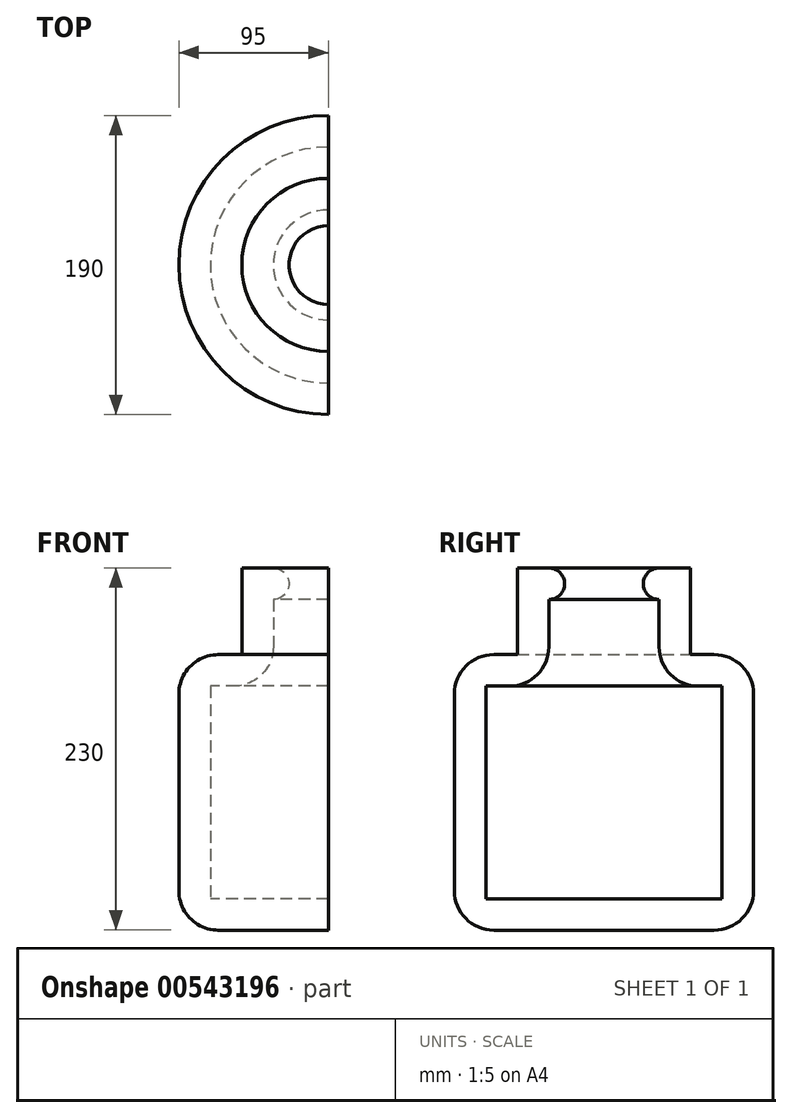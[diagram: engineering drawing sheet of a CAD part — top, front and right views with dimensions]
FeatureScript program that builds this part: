
annotation { "Feature Type Name" : "Feature", "Feature Type Description" : "" }
export const myFeature = defineFeature(function(context is Context, id is Id, definition is map)
    precondition{}
    {
        {
            var Q0;
            Q0=qCreatedBy(makeId("Front.planeOp"),FACE);
            var sketch = newSketch(context, id + "F0", { "sketchPlane" : qUnion([Q0])});
            skLineSegment(sketch, "E0", {"start": v(-40, 68.66) * mm, "end": v(-40, -56.34) * mm});
            skLineSegment(sketch, "E1", {"start": v(-15, -81.34) * mm, "end": v(55, -81.34) * mm});
            skLineSegment(sketch, "E2", {"start": v(55, -81.34) * mm, "end": v(55, -61.34) * mm});
            skLineSegment(sketch, "E3", {"start": v(55, -61.34) * mm, "end": v(-20, -61.34) * mm});
            skLineSegment(sketch, "E4", {"start": v(-20, -61.34) * mm, "end": v(-20, 73.66) * mm});
            skLineSegment(sketch, "E5", {"start": v(-20, 73.66) * mm, "end": v(-5, 73.66) * mm});
            skLineSegment(sketch, "E6", {"start": v(-15, 93.66) * mm, "end": v(0, 93.66) * mm});
            skLineSegment(sketch, "E7", {"start": v(0, 93.66) * mm, "end": v(0, 148.66) * mm});
            skLineSegment(sketch, "E8", {"start": v(0, 148.66) * mm, "end": v(20, 148.66) * mm});
            skLineSegment(sketch, "E9", {"start": v(20, 98.66) * mm, "end": v(20, 128.66) * mm});
            skArc(sketch, "E10", {"start": v(20, 128.66) * mm, "mid": v(30, 138.66) * mm, "end": v(20, 148.66) * mm});
            skPoint(sketch, "E11.visualSharp", {"position": v(-40, 93.66) * mm});
            skArc(sketch, "E11.filletArc", {"start": v(-15, 93.66) * mm, "mid": v(-32.68, 86.34) * mm, "end": v(-40, 68.66) * mm});
            skPoint(sketch, "E12.visualSharp", {"position": v(-40, -81.34) * mm});
            skArc(sketch, "E12.filletArc", {"start": v(-40, -56.34) * mm, "mid": v(-32.68, -74.02) * mm, "end": v(-15, -81.34) * mm});
            skPoint(sketch, "E13.visualSharp", {"position": v(20, 73.66) * mm});
            skArc(sketch, "E13.filletArc", {"start": v(-5, 73.66) * mm, "mid": v(12.68, 80.98) * mm, "end": v(20, 98.66) * mm});
            skSolve(sketch);
        }
        {
            var Q0;
            Q0=makeQuery(id+"F0.imprint","IMPRINT",FACE,{"disambiguationData":[TD([[makeQuery(id+"F0.imprint","IMPRINT",EDGE,{"derivedFrom":sQuery(id+"F0.wireOp",EDGE,"E0")}),1.0]])]});
            var Q1;
            Q1=sQuery(id+"F0.wireOp",EDGE,"E2");
            revolve(context, id + "F1", {"entities" : qUnion([Q0]), "axis" : qUnion([Q1]), "revolveType" : RevolveType.SYMMETRIC, "angle" : 180 * degree});
        }
    });
